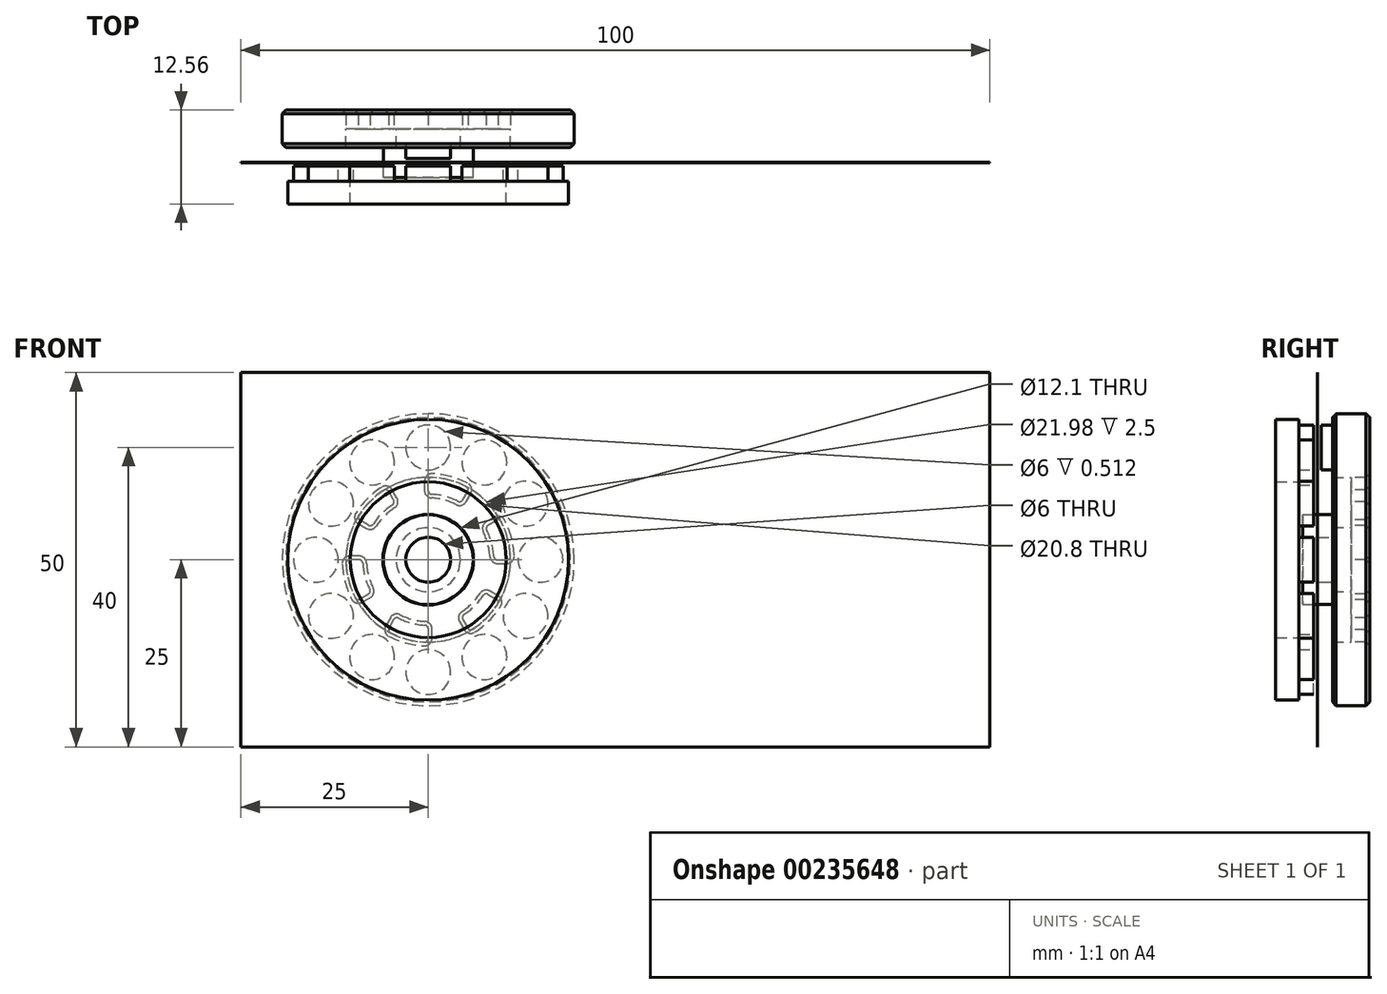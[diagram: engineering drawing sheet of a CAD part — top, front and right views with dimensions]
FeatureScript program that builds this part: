
annotation { "Feature Type Name" : "Feature", "Feature Type Description" : "" }
export const myFeature = defineFeature(function(context is Context, id is Id, definition is map)
    precondition{}
    {
        {
            var Q0;
            Q0=qCreatedBy(makeId("Front.planeOp"),FACE);
            var sketch = newSketch(context, id + "F0", { "sketchPlane" : qUnion([Q0])});
            skLineSegment(sketch, "E0.bottom", {"start": v(-25, 25) * mm, "end": v(75, 25) * mm});
            skLineSegment(sketch, "E0.top", {"start": v(-25, -25) * mm, "end": v(75, -25) * mm});
            skLineSegment(sketch, "E0.left", {"start": v(-25, 25) * mm, "end": v(-25, -25) * mm});
            skLineSegment(sketch, "E0.right", {"start": v(75, 25) * mm, "end": v(75, -25) * mm});
            skCircle(sketch, "E1", {"center": v(0, 0) * mm, "radius": 6.05 * mm});
            skSolve(sketch);
        }
        {
            var Q0;
            Q0 = qSketchRegion(id + "F0", true);
            extrude(context, id + "F1", {"entities" : qUnion([Q0]), "depth" : .63 / 50.8 * mm, "hasSecondDirection" : true, "secondDirectionOppositeDirection" : true, "secondDirectionDepth" : .63 / 50.8 * mm});
        }
        {
            var Q0;
            Q0=makeQuery(id+"F1.opExtrude","CAP_FACE",FACE,{"disambiguationData":[OSD([sQuery(id+"F0.wireOp",EDGE,"E0.bottom"),sQuery(id+"F0.wireOp",EDGE,"E0.top"),sQuery(id+"F0.wireOp",EDGE,"E0.left"),sQuery(id+"F0.wireOp",EDGE,"E0.right"),sQuery(id+"F0.wireOp",EDGE,"E1")])],"isStart":false});
            cPlane(context, id + "F2", {"entities" : qUnion([Q0]), "cplaneType" : CPlaneType.OFFSET, "offset" : .5 * mm, "width" : 150 * mm, "height" : 150 * mm});
        }
        {
            var Q0;
            Q0=qCreatedBy(id+"F2.planeOp",FACE);
            var sketch = newSketch(context, id + "F3", { "sketchPlane" : qUnion([Q0])});
            skCircle(sketch, "E2", {"center": v(0, 15) * mm, "radius": 3 * mm});
            skCircle(sketch, "E3.1.0", {"center": v(-7.5, 13) * mm, "radius": 3 * mm});
            skCircle(sketch, "E3.2.0", {"center": v(-13, 7.5) * mm, "radius": 3 * mm});
            skPoint(sketch, "E3.center", {"position": v(0, 0) * mm});
            skCircle(sketch, "E4.1.3.0", {"center": v(-15, 0) * mm, "radius": 3 * mm});
            skCircle(sketch, "E4.1.4.0", {"center": v(-13, -7.5) * mm, "radius": 3 * mm});
            skCircle(sketch, "E4.1.5.0", {"center": v(-7.5, -13) * mm, "radius": 3 * mm});
            skCircle(sketch, "E4.1.6.0", {"center": v(0, -15) * mm, "radius": 3 * mm});
            skCircle(sketch, "E4.1.7.0", {"center": v(7.5, -13) * mm, "radius": 3 * mm});
            skCircle(sketch, "E5.1.8.0", {"center": v(13, -7.5) * mm, "radius": 3 * mm});
            skCircle(sketch, "E5.1.9.0", {"center": v(15, 0) * mm, "radius": 3 * mm});
            skCircle(sketch, "E5.1.10.0", {"center": v(13, 7.5) * mm, "radius": 3 * mm});
            skCircle(sketch, "E5.1.11.0", {"center": v(7.5, 13) * mm, "radius": 3 * mm});
            skSolve(sketch);
        }
        {
            var Q0;
            Q0 = qSketchRegion(id + "F3", true);
            extrude(context, id + "F4", {"entities" : qUnion([Q0]), "depth" : 2 * mm});
        }
        {
            var Q0;
            Q0=makeQuery(id+"F4.opExtrude","CAP_FACE",FACE,{"disambiguationData":[OSD([sQuery(id+"F3.wireOp",EDGE,"E2")])],"isStart":false});
            var sketch = newSketch(context, id + "F5", { "sketchPlane" : qUnion([Q0])});
            skCircle(sketch, "E6", {"center": v(0, 0) * mm, "radius": 10.4 * mm});
            skCircle(sketch, "E7", {"center": v(0, 0) * mm, "radius": 18.75 * mm});
            skSolve(sketch);
        }
        {
            var Q0;
            Q0 = qSketchRegion(id + "F5", true);
            extrude(context, id + "F6", {"entities" : qUnion([Q0]), "depth" : 3.05 * mm});
        }
        {
            var Q0;
            Q0=makeQuery(id+"F4.opExtrude","SWEPT_BODY",BODY,{"disambiguationData":[OSD([sQuery(id+"F3.wireOp",EDGE,"E2")])]});
            var Q1;
            Q1=qCreatedBy(makeId("Front.planeOp"),FACE);
            mirror(context, id + "F7", {"entities" : qUnion([Q0]), "mirrorPlane" : qUnion([Q1])});
        }
        {
            var Q0;
            Q0=qCreatedBy(makeId("Front.planeOp"),FACE);
            var sketch = newSketch(context, id + "F8", { "sketchPlane" : qUnion([Q0])});
            skCircle(sketch, "E8", {"center": v(0, 0) * mm, "radius": 6 * mm});
            skCircle(sketch, "E9", {"center": v(0, 0) * mm, "radius": 3 * mm});
            skSolve(sketch);
        }
        {
            var Q0;
            Q0 = qSketchRegion(id + "F8", true);
            extrude(context, id + "F9", {"entities" : qUnion([Q0]), "depth" : 2 * mm, "hasSecondDirection" : true, "secondDirectionOppositeDirection" : true, "secondDirectionDepth" : 2 * mm});
        }
        {
            var Q0;
            Q0=qCreatedBy(makeId("Top.planeOp"),FACE);
            var sketch = newSketch(context, id + "F10", { "sketchPlane" : qUnion([Q0])});
            skLineSegment(sketch, "E10", {"start": v(-19.5, 2.5) * mm, "end": v(-19.5, 6.5) * mm});
            skLineSegment(sketch, "E11", {"start": v(-19, 7) * mm, "end": v(0, 7) * mm});
            skLineSegment(sketch, "E12", {"start": v(-11, 2) * mm, "end": v(-11, 4.5) * mm});
            skLineSegment(sketch, "E13.0", {"start": v(-3, 0) * mm, "end": v(-3, 2) * mm});
            skLineSegment(sketch, "E14", {"start": v(-11, 4.5) * mm, "end": v(-4.29, 4.5) * mm});
            skLineSegment(sketch, "E15", {"start": v(0, 0) * mm, "end": v(-3, 0) * mm});
            skLineSegment(sketch, "E16.0", {"start": v(-3, 2) * mm, "end": v(-4.29, 2) * mm});
            skLineSegment(sketch, "E17", {"start": v(-4.29, 4.5) * mm, "end": v(-4.29, 2) * mm});
            skLineSegment(sketch, "E18.trimOffspring", {"start": v(-11, 2) * mm, "end": v(-19, 2) * mm});
            skLineSegment(sketch, "E19", {"start": v(-3, 0) * mm, "end": v(0, 0) * mm});
            skLineSegment(sketch, "E20", {"start": v(0, 7) * mm, "end": v(0, 0) * mm});
            skPoint(sketch, "E21.visualSharp", {"position": v(-19.5, 7) * mm});
            skPoint(sketch, "E22.visualSharp", {"position": v(-19.5, 2) * mm});
            skLineSegment(sketch, "E23", {"start": v(-19, 7) * mm, "end": v(-19.5, 6.5) * mm});
            skLineSegment(sketch, "E24", {"start": v(-19.5, 2.5) * mm, "end": v(-19, 2) * mm});
            skSolve(sketch);
        }
        {
            var Q0;
            Q0 = qSketchRegion(id + "F10", true);
            var Q1;
            Q1=sQuery(id+"F10.wireOp",EDGE,"E20");
            revolve(context, id + "F11", {"entities" : qUnion([Q0]), "axis" : qUnion([Q1]), "revolveType" : RevolveType.FULL});
        }
        {
            var Q0;
            Q0=makeQuery(id+"F7.opPattern","COPY",BODY,{"derivedFrom":makeQuery(id+"F4.opExtrude","SWEPT_BODY",BODY,{"disambiguationData":[OSD([sQuery(id+"F3.wireOp",EDGE,"E2")])]}),"instanceName":"1"});
            var Q1;
            Q1=makeQuery(id+"F11.opRevolve","SWEPT_BODY",BODY,{"disambiguationData":[OSD([sQuery(id+"F10.wireOp",EDGE,"E10"),sQuery(id+"F10.wireOp",EDGE,"E11"),sQuery(id+"F10.wireOp",EDGE,"E12"),sQuery(id+"F10.wireOp",EDGE,"E13.0"),sQuery(id+"F10.wireOp",EDGE,"E14"),sQuery(id+"F10.wireOp",EDGE,"E16.0"),sQuery(id+"F10.wireOp",EDGE,"E17"),sQuery(id+"F10.wireOp",EDGE,"E18.trimOffspring"),sQuery(id+"F10.wireOp",EDGE,"E19"),sQuery(id+"F10.wireOp",EDGE,"E20"),sQuery(id+"F10.wireOp",EDGE,"E21.filletArc"),sQuery(id+"F10.wireOp",EDGE,"E22.filletArc")])]});
            booleanBodies(context, id + "F12", {"operationType" : BooleanOperationType.SUBTRACTION, "tools" : qUnion([Q0]), "targets" : qUnion([Q1]), "keepTools" : true});
        }
        {
            var Q0;
            Q0=makeQuery(id+"F11.opRevolve","SWEPT_FACE",FACE,{"disambiguationData":[OSD([sQuery(id+"F10.wireOp",EDGE,"E14")])]});
            var sketch = newSketch(context, id + "F13", { "sketchPlane" : qUnion([Q0])});
            skArc(sketch, "E25", {"start": v(5.04, 9.78) * mm, "mid": v(2.85, 10.63) * mm, "end": v(0.52, 10.99) * mm});
            skArc(sketch, "E26", {"start": v(3.96, 7.8) * mm, "mid": v(2.26, 8.45) * mm, "end": v(0.47, 8.74) * mm});
            skLineSegment(sketch, "E27", {"start": v(0, 9.24) * mm, "end": v(0, 10.49) * mm});
            skLineSegment(sketch, "E28", {"start": v(4.62, 8) * mm, "end": v(5.24, 9.08) * mm});
            skPoint(sketch, "E29.visualSharp", {"position": v(0, 11) * mm});
            skArc(sketch, "E29.filletArc", {"start": v(0.52, 10.99) * mm, "mid": v(0.15, 10.85) * mm, "end": v(0, 10.49) * mm});
            skPoint(sketch, "E30.visualSharp", {"position": v(0, 8.75) * mm});
            skArc(sketch, "E30.filletArc", {"start": v(0, 9.24) * mm, "mid": v(0.14, 8.9) * mm, "end": v(0.47, 8.74) * mm});
            skPoint(sketch, "E31.visualSharp", {"position": v(4.38, 7.58) * mm});
            skArc(sketch, "E31.filletArc", {"start": v(3.96, 7.8) * mm, "mid": v(4.33, 7.77) * mm, "end": v(4.62, 8) * mm});
            skPoint(sketch, "E32.visualSharp", {"position": v(5.5, 9.53) * mm});
            skArc(sketch, "E32.filletArc", {"start": v(5.24, 9.08) * mm, "mid": v(5.3, 9.47) * mm, "end": v(5.04, 9.78) * mm});
            skArc(sketch, "E33.1.0", {"start": v(-5.95, 9.25) * mm, "mid": v(-7.78, 7.78) * mm, "end": v(-9.25, 5.95) * mm});
            skArc(sketch, "E33.1.1", {"start": v(-9.25, 5.95) * mm, "mid": v(-9.32, 5.56) * mm, "end": v(-9.08, 5.24) * mm});
            skLineSegment(sketch, "E33.1.2", {"start": v(-8, 4.62) * mm, "end": v(-9.08, 5.24) * mm});
            skArc(sketch, "E33.1.3", {"start": v(-8, 4.62) * mm, "mid": v(-7.63, 4.56) * mm, "end": v(-7.33, 4.78) * mm});
            skArc(sketch, "E33.1.4", {"start": v(-4.78, 7.33) * mm, "mid": v(-6.19, 6.19) * mm, "end": v(-7.33, 4.78) * mm});
            skArc(sketch, "E33.1.5", {"start": v(-4.78, 7.33) * mm, "mid": v(-4.56, 7.63) * mm, "end": v(-4.62, 8) * mm});
            skLineSegment(sketch, "E33.1.6", {"start": v(-4.62, 8) * mm, "end": v(-5.24, 9.08) * mm});
            skArc(sketch, "E33.1.7", {"start": v(-5.24, 9.08) * mm, "mid": v(-5.56, 9.32) * mm, "end": v(-5.95, 9.25) * mm});
            skArc(sketch, "E33.2.0", {"start": v(-10.99, -0.52) * mm, "mid": v(-10.63, -2.85) * mm, "end": v(-9.78, -5.04) * mm});
            skArc(sketch, "E33.2.1", {"start": v(-9.78, -5.04) * mm, "mid": v(-9.47, -5.3) * mm, "end": v(-9.08, -5.24) * mm});
            skLineSegment(sketch, "E33.2.2", {"start": v(-8, -4.62) * mm, "end": v(-9.08, -5.24) * mm});
            skArc(sketch, "E33.2.3", {"start": v(-8, -4.62) * mm, "mid": v(-7.77, -4.33) * mm, "end": v(-7.8, -3.96) * mm});
            skArc(sketch, "E33.2.4", {"start": v(-8.74, -0.47) * mm, "mid": v(-8.45, -2.26) * mm, "end": v(-7.8, -3.96) * mm});
            skArc(sketch, "E33.2.5", {"start": v(-8.74, -0.47) * mm, "mid": v(-8.9, -0.14) * mm, "end": v(-9.24, 0) * mm});
            skLineSegment(sketch, "E33.2.6", {"start": v(-9.24, 0) * mm, "end": v(-10.49, 0) * mm});
            skArc(sketch, "E33.2.7", {"start": v(-10.49, 0) * mm, "mid": v(-10.85, -0.15) * mm, "end": v(-10.99, -0.52) * mm});
            skArc(sketch, "E34.3.3.0", {"start": v(-5.04, -9.78) * mm, "mid": v(-2.85, -10.63) * mm, "end": v(-0.52, -10.99) * mm});
            skArc(sketch, "E34.4.3.0", {"start": v(-0.52, -10.99) * mm, "mid": v(-0.15, -10.85) * mm, "end": v(0, -10.49) * mm});
            skLineSegment(sketch, "E34.8.3.0", {"start": v(0, -9.24) * mm, "end": v(0, -10.49) * mm});
            skArc(sketch, "E34.11.3.0", {"start": v(0, -9.24) * mm, "mid": v(-0.14, -8.9) * mm, "end": v(-0.47, -8.74) * mm});
            skArc(sketch, "E34.15.3.0", {"start": v(-3.96, -7.8) * mm, "mid": v(-2.26, -8.45) * mm, "end": v(-0.47, -8.74) * mm});
            skArc(sketch, "E34.19.3.0", {"start": v(-3.96, -7.8) * mm, "mid": v(-4.33, -7.77) * mm, "end": v(-4.62, -8) * mm});
            skLineSegment(sketch, "E34.23.3.0", {"start": v(-4.62, -8) * mm, "end": v(-5.24, -9.08) * mm});
            skArc(sketch, "E34.26.3.0", {"start": v(-5.24, -9.08) * mm, "mid": v(-5.3, -9.47) * mm, "end": v(-5.04, -9.78) * mm});
            skArc(sketch, "E34.3.4.0", {"start": v(5.95, -9.25) * mm, "mid": v(7.78, -7.78) * mm, "end": v(9.25, -5.95) * mm});
            skArc(sketch, "E34.4.4.0", {"start": v(9.25, -5.95) * mm, "mid": v(9.32, -5.56) * mm, "end": v(9.08, -5.24) * mm});
            skLineSegment(sketch, "E34.8.4.0", {"start": v(8, -4.62) * mm, "end": v(9.08, -5.24) * mm});
            skArc(sketch, "E34.11.4.0", {"start": v(8, -4.62) * mm, "mid": v(7.63, -4.56) * mm, "end": v(7.33, -4.78) * mm});
            skArc(sketch, "E34.15.4.0", {"start": v(4.78, -7.33) * mm, "mid": v(6.19, -6.19) * mm, "end": v(7.33, -4.78) * mm});
            skArc(sketch, "E34.19.4.0", {"start": v(4.78, -7.33) * mm, "mid": v(4.56, -7.63) * mm, "end": v(4.62, -8) * mm});
            skLineSegment(sketch, "E34.23.4.0", {"start": v(4.62, -8) * mm, "end": v(5.24, -9.08) * mm});
            skArc(sketch, "E34.26.4.0", {"start": v(5.24, -9.08) * mm, "mid": v(5.56, -9.32) * mm, "end": v(5.95, -9.25) * mm});
            skArc(sketch, "E34.3.5.0", {"start": v(10.99, 0.52) * mm, "mid": v(10.63, 2.85) * mm, "end": v(9.78, 5.04) * mm});
            skArc(sketch, "E34.4.5.0", {"start": v(9.78, 5.04) * mm, "mid": v(9.47, 5.3) * mm, "end": v(9.08, 5.24) * mm});
            skLineSegment(sketch, "E34.8.5.0", {"start": v(8, 4.62) * mm, "end": v(9.08, 5.24) * mm});
            skArc(sketch, "E34.11.5.0", {"start": v(8, 4.62) * mm, "mid": v(7.77, 4.33) * mm, "end": v(7.8, 3.96) * mm});
            skArc(sketch, "E34.15.5.0", {"start": v(8.74, 0.47) * mm, "mid": v(8.45, 2.26) * mm, "end": v(7.8, 3.96) * mm});
            skArc(sketch, "E34.19.5.0", {"start": v(8.74, 0.47) * mm, "mid": v(8.9, 0.14) * mm, "end": v(9.24, 0) * mm});
            skLineSegment(sketch, "E34.23.5.0", {"start": v(9.24, 0) * mm, "end": v(10.49, 0) * mm});
            skArc(sketch, "E34.26.5.0", {"start": v(10.49, 0) * mm, "mid": v(10.85, 0.15) * mm, "end": v(10.99, 0.52) * mm});
            skSolve(sketch);
        }
        {
            var Q0;
            Q0 = qSketchRegion(id + "F13", true);
            extrude(context, id + "F14", {"entities" : qUnion([Q0]), "operationType" : NewBodyOperationType.REMOVE, "oppositeDirection" : true, "depth" : 3 * mm});
        }
        {
            var Q0;
            Q0=makeQuery(id+"F14.boolean.opBoolean","INTERSECT",EDGE,{"derivedFrom":[makeQuery(id+"F11.opRevolve","SWEPT_FACE",FACE,{"disambiguationData":[OSD([sQuery(id+"F10.wireOp",EDGE,"E11")])]}),makeQuery(id+"F14.opExtrude","SWEPT_FACE",FACE,{"disambiguationData":[OSD([sQuery(id+"F13.wireOp",EDGE,"E33.1.6")])]})]});
            var Q1;
            Q1=makeQuery(id+"F14.boolean.opBoolean","INTERSECT",EDGE,{"derivedFrom":[makeQuery(id+"F11.opRevolve","SWEPT_FACE",FACE,{"disambiguationData":[OSD([sQuery(id+"F10.wireOp",EDGE,"E11")])]}),makeQuery(id+"F14.opExtrude","SWEPT_FACE",FACE,{"disambiguationData":[OSD([sQuery(id+"F13.wireOp",EDGE,"E25")])]})]});
            var Q2;
            Q2=makeQuery(id+"F14.boolean.opBoolean","INTERSECT",EDGE,{"derivedFrom":[makeQuery(id+"F11.opRevolve","SWEPT_FACE",FACE,{"disambiguationData":[OSD([sQuery(id+"F10.wireOp",EDGE,"E11")])]}),makeQuery(id+"F14.opExtrude","SWEPT_FACE",FACE,{"disambiguationData":[OSD([sQuery(id+"F13.wireOp",EDGE,"E34.3.5.0")])]})]});
            var Q3;
            Q3=makeQuery(id+"F14.boolean.opBoolean","INTERSECT",EDGE,{"derivedFrom":[makeQuery(id+"F11.opRevolve","SWEPT_FACE",FACE,{"disambiguationData":[OSD([sQuery(id+"F10.wireOp",EDGE,"E11")])]}),makeQuery(id+"F14.opExtrude","SWEPT_FACE",FACE,{"disambiguationData":[OSD([sQuery(id+"F13.wireOp",EDGE,"E34.8.4.0")])]})]});
            var Q4;
            Q4=makeQuery(id+"F14.boolean.opBoolean","INTERSECT",EDGE,{"derivedFrom":[makeQuery(id+"F11.opRevolve","SWEPT_FACE",FACE,{"disambiguationData":[OSD([sQuery(id+"F10.wireOp",EDGE,"E11")])]}),makeQuery(id+"F14.opExtrude","SWEPT_FACE",FACE,{"disambiguationData":[OSD([sQuery(id+"F13.wireOp",EDGE,"E34.15.3.0")])]})]});
            var Q5;
            Q5=makeQuery(id+"F14.boolean.opBoolean","INTERSECT",EDGE,{"derivedFrom":[makeQuery(id+"F11.opRevolve","SWEPT_FACE",FACE,{"disambiguationData":[OSD([sQuery(id+"F10.wireOp",EDGE,"E11")])]}),makeQuery(id+"F14.opExtrude","SWEPT_FACE",FACE,{"disambiguationData":[OSD([sQuery(id+"F13.wireOp",EDGE,"E33.2.4")])]})]});
            var Q6;
            Q6=makeQuery(id+"F14.boolean.opBoolean","COPY",EDGE,{"derivedFrom":makeQuery(id+"F14.opExtrude","CAP_EDGE",EDGE,{"disambiguationData":[OSD([sQuery(id+"F13.wireOp",EDGE,"E33.2.4")])],"isStart":true})});
            var Q7;
            Q7=makeQuery(id+"F14.boolean.opBoolean","COPY",EDGE,{"derivedFrom":makeQuery(id+"F14.opExtrude","CAP_EDGE",EDGE,{"disambiguationData":[OSD([sQuery(id+"F13.wireOp",EDGE,"E34.15.3.0")])],"isStart":true})});
            var Q8;
            Q8=makeQuery(id+"F14.boolean.opBoolean","COPY",EDGE,{"derivedFrom":makeQuery(id+"F14.opExtrude","CAP_EDGE",EDGE,{"disambiguationData":[OSD([sQuery(id+"F13.wireOp",EDGE,"E34.15.4.0")])],"isStart":true})});
            var Q9;
            Q9=makeQuery(id+"F14.boolean.opBoolean","COPY",EDGE,{"derivedFrom":makeQuery(id+"F14.opExtrude","CAP_EDGE",EDGE,{"disambiguationData":[OSD([sQuery(id+"F13.wireOp",EDGE,"E34.15.5.0")])],"isStart":true})});
            var Q10;
            Q10=makeQuery(id+"F14.boolean.opBoolean","COPY",EDGE,{"derivedFrom":makeQuery(id+"F14.opExtrude","CAP_EDGE",EDGE,{"disambiguationData":[OSD([sQuery(id+"F13.wireOp",EDGE,"E26")])],"isStart":true})});
            var Q11;
            Q11=makeQuery(id+"F14.boolean.opBoolean","COPY",EDGE,{"derivedFrom":makeQuery(id+"F14.opExtrude","CAP_EDGE",EDGE,{"disambiguationData":[OSD([sQuery(id+"F13.wireOp",EDGE,"E33.1.4")])],"isStart":true})});
            chamfer(context, id + "F15", {"entities" : qUnion([Q0, Q1, Q2, Q3, Q4, Q5, Q6, Q7, Q8, Q9, Q10, Q11]), "width" : .5 * mm, "tangentPropagation" : true});
        }
    });
